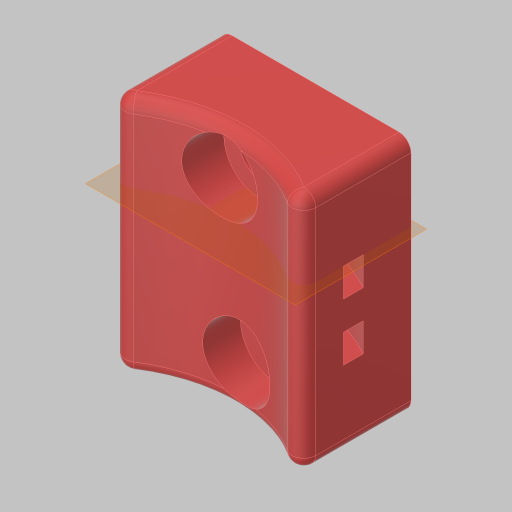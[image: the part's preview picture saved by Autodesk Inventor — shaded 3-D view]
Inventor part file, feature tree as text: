
AUTODESK INVENTOR PART (.ipt)
format: ipt  version: 2023.5 (Build 275446000, 446)  size: 215,552 bytes
history: native  units: in
note: dims shown in document units (in); Inventor stores cm internally (conversion verified against a paired STEP export)
features: sketch x4, extrude x3, plane x2, hole x1, mirror x1, fillet x1, projected_geometry x1
ambient origin geometry x8: Origin, YZ Plane, XZ Plane, XY Plane, X Axis, Y Axis, Z Axis, Center Point
bodies: Solid1 (feature_tree)
feature tree (13):
  sketch  "Sketch1"  dims[d0=1.25in d1=1.0in]
  extrude  "Extrusion1"  Depth=1.0in
  extrude  "Extrusion2"  Depth=0.7942in
  plane  "Work Plane1"
  hole  "Hole2"  [1 undecoded]
  plane  "Work Plane2"
  extrude  "Extrusion3"  TaperAngle=0.0deg  [1 undecoded]
  mirror  "Mirror1"
  fillet  "Fillet1"  [1 undecoded]
  sketch  "Sketch2"  dims[d2=0.0871in d3=0.7942in]
  projected_geometry  "Projected Loop1"
  sketch  "Sketch3"  dims[d4=0.75in d5=0.0in d13=0.75in]
  sketch  "Sketch5"  dims[d14=0.125in d15=0.0in d16=0.0in d17=-0.44in d18=0.201in d19=0.75in d20=0.375in d21=0.19in d22=0.5635in d23=1.0in d24=0.8108in d28=-0.4in d29=0.09in d30=0.25in d31=0.15in d32=0.0in d33=0.0625in]
note: 3 required parameter values undecoded (feature->parameter linkage not recoverable at this tier; creation-order binding heuristic only, values carry confidence <= 0.55)
